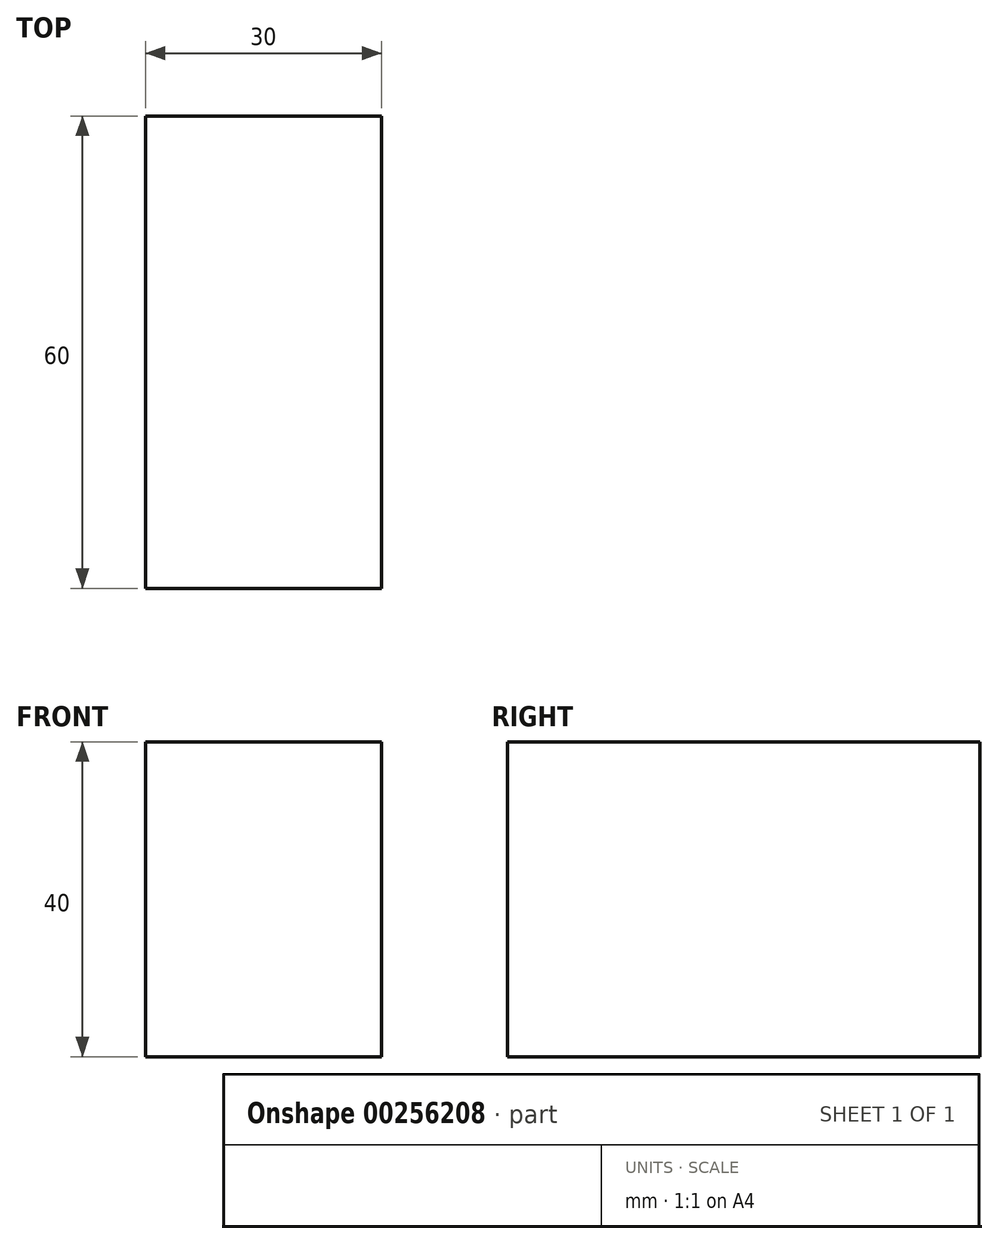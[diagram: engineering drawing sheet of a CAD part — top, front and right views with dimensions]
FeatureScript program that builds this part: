
annotation { "Feature Type Name" : "Feature", "Feature Type Description" : "" }
export const myFeature = defineFeature(function(context is Context, id is Id, definition is map)
    precondition{}
    {
        {
            var Q0;
            Q0=qCreatedBy(makeId("Right.planeOp"),FACE);
            var sketch = newSketch(context, id + "F0", { "sketchPlane" : qUnion([Q0])});
            skLineSegment(sketch, "E0.bottom", {"start": v(0, 0) * mm, "end": v(60, 0) * mm});
            skLineSegment(sketch, "E0.top", {"start": v(0, -40) * mm, "end": v(60, -40) * mm});
            skLineSegment(sketch, "E0.left", {"start": v(0, 0) * mm, "end": v(0, -40) * mm});
            skLineSegment(sketch, "E0.right", {"start": v(60, 0) * mm, "end": v(60, -40) * mm});
            skSolve(sketch);
        }
        {
            var Q0;
            Q0 = qSketchRegion(id + "F0", true);
            extrude(context, id + "F1", {"entities" : qUnion([Q0]), "depth" : 30 * mm});
        }
    });
